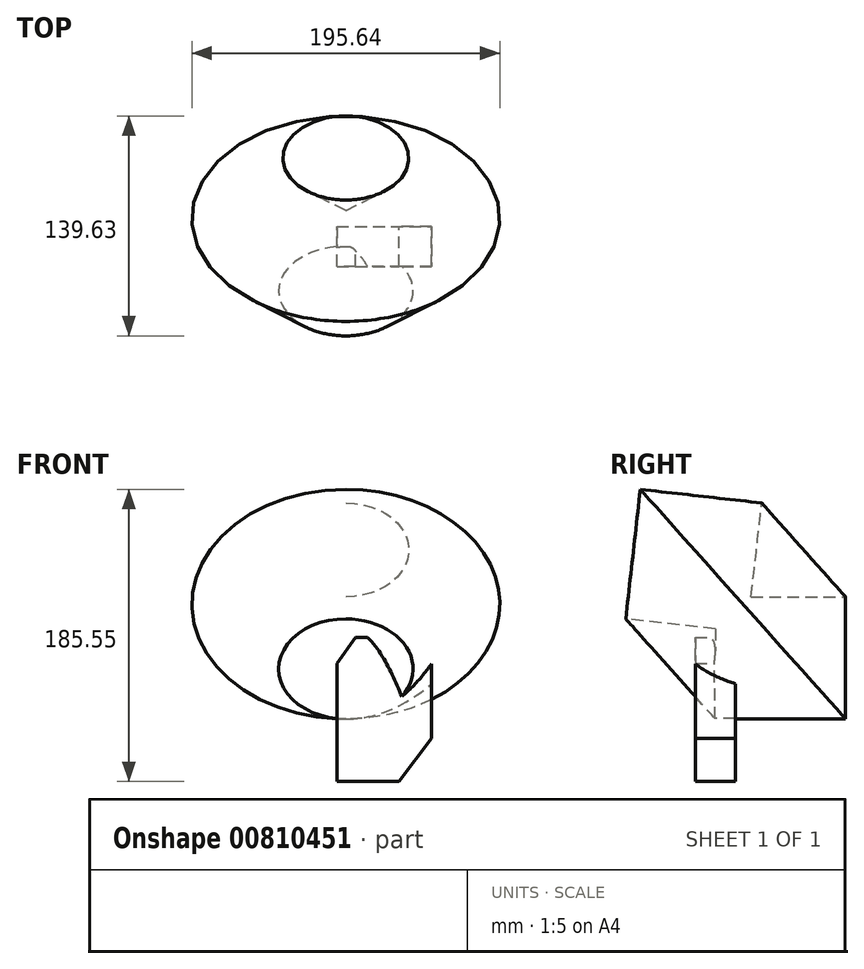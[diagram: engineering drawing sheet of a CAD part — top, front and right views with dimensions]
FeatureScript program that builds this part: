
annotation { "Feature Type Name" : "Feature", "Feature Type Description" : "" }
export const myFeature = defineFeature(function(context is Context, id is Id, definition is map)
    precondition{}
    {
        {
            var Q0;
            Q0=qCreatedBy(makeId("Front.planeOp"),FACE);
            var sketch = newSketch(context, id + "F0", { "sketchPlane" : qUnion([Q0])});
            skLineSegment(sketch, "E0.bottom", {"start": v(-5.65, 36.19) * mm, "end": v(54.51, 36.19) * mm});
            skLineSegment(sketch, "E0.top", {"start": v(-5.65, -55.43) * mm, "end": v(54.51, -55.43) * mm});
            skLineSegment(sketch, "E0.left", {"start": v(-5.65, 36.19) * mm, "end": v(-5.65, -55.43) * mm});
            skLineSegment(sketch, "E0.right", {"start": v(54.51, 36.19) * mm, "end": v(54.51, -55.43) * mm});
            skLineSegment(sketch, "E1", {"start": v(23.06, 59.7) * mm, "end": v(-19.7, 0) * mm});
            skLineSegment(sketch, "E2", {"start": v(67.64, -10.84) * mm, "end": v(23.97, -68.25) * mm});
            skSolve(sketch);
        }
        {
            var Q0;
            {var subQ7=sQuery(id+"F0.wireOp",EDGE,"E0.right");var subQ8=sQuery(id+"F0.wireOp",EDGE,"E0.bottom");var subQ9=makeQuery(id+"F0.imprint","INTERSECT",VERTEX,{"derivedFrom":[subQ8,subQ7]});Q0=makeQuery(id+"F0.imprint","IMPRINT",FACE,{"disambiguationData":[TD([[makeQuery(id+"F0.imprint","IMPRINT",EDGE,{"disambiguationData":[TD([[subQ9,1.0]])],"derivedFrom":subQ8}),-1.0]])]});}
            extrude(context, id + "F1", {"entities" : qUnion([Q0]), "depth" : 25.4 * mm, "offsetDistance" : 25.4 * mm});
        }
        {
            var Q0;
            Q0=qCreatedBy(makeId("Right.planeOp"),FACE);
            var sketch = newSketch(context, id + "F2", { "sketchPlane" : qUnion([Q0])});
            skLineSegment(sketch, "E3.bottom", {"start": v(-12.67, 61.84) * mm, "end": v(70.09, 61.84) * mm});
            skLineSegment(sketch, "E3.top", {"start": v(-12.67, -15.73) * mm, "end": v(70.09, -15.73) * mm});
            skLineSegment(sketch, "E3.left", {"start": v(-12.67, 61.84) * mm, "end": v(-12.67, -15.73) * mm});
            skLineSegment(sketch, "E3.right", {"start": v(70.09, 61.84) * mm, "end": v(70.09, -15.73) * mm});
            skLineSegment(sketch, "E4", {"start": v(21.56, 72.1) * mm, "end": v(-29.73, 26.25) * mm});
            skSolve(sketch);
        }
        {
            var Q0;
            {var subQ2=sQuery(id+"F2.wireOp",EDGE,"E3.top");Q0=makeQuery(id+"F2.imprint","IMPRINT",FACE,{"disambiguationData":[TD([[makeQuery(id+"F2.imprint","IMPRINT",EDGE,{"derivedFrom":subQ2}),1.0]])]});}
            var Q1;
            Q1=sQuery(id+"F2.wireOp",EDGE,"E4");
            revolve(context, id + "F3", {"operationType" : NewBodyOperationType.ADD, "surfaceOperationType" : NewSurfaceOperationType.NEW, "entities" : qUnion([Q0]), "axis" : qUnion([Q1]), "revolveType" : RevolveType.FULL});
        }
    });
